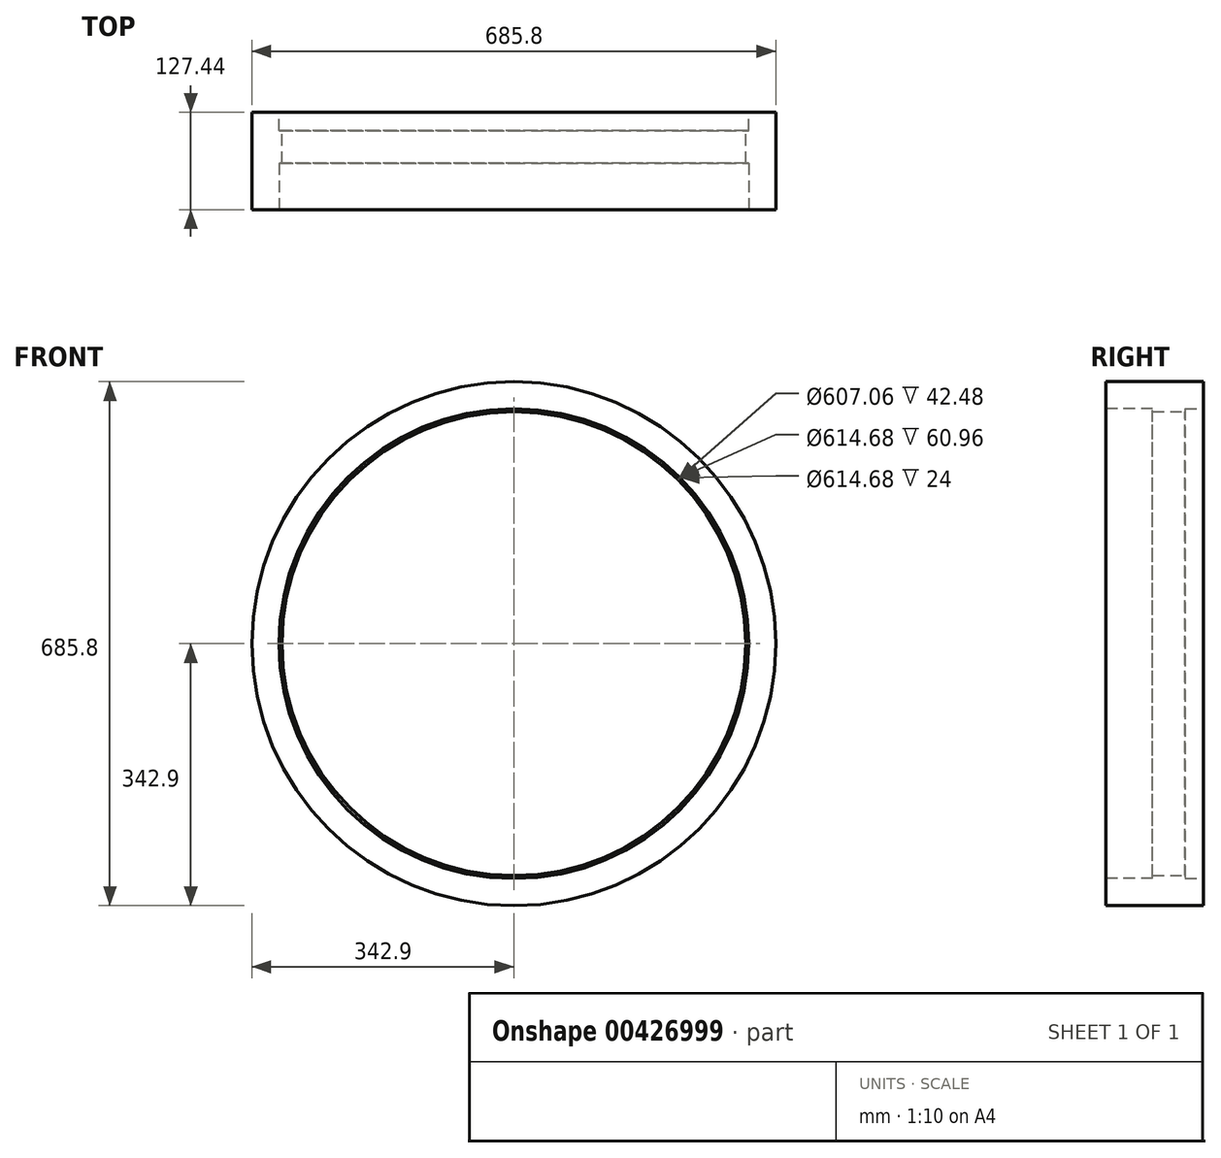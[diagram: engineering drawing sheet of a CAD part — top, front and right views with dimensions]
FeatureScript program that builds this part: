
annotation { "Feature Type Name" : "Feature", "Feature Type Description" : "" }
export const myFeature = defineFeature(function(context is Context, id is Id, definition is map)
    precondition{}
    {
        {
            var Q0;
            Q0=qCreatedBy(makeId("Front.planeOp"),FACE);
            var sketch = newSketch(context, id + "F0", { "sketchPlane" : qUnion([Q0])});
            skCircle(sketch, "E0", {"center": v(0, 0) * mm, "radius": 342.9 * mm});
            skCircle(sketch, "E1", {"center": v(0, 0) * mm, "radius": 303.53 * mm});
            skSolve(sketch);
        }
        {
            var Q0;
            Q0=makeQuery(id+"F0.imprint","IMPRINT",FACE,{"disambiguationData":[TD([[makeQuery(id+"F0.imprint","IMPRINT",EDGE,{"derivedFrom":sQuery(id+"F0.wireOp",EDGE,"E0")}),1.0]])]});
            extrude(context, id + "F1", {"entities" : qUnion([Q0]), "depth" : 91.44 * mm, "hasSecondDirection" : true, "secondDirectionOppositeDirection" : true, "secondDirectionDepth" : 36 * mm});
        }
        {
            var Q0;
            Q0=makeQuery(id+"F1.opExtrude","CAP_FACE",FACE,{"disambiguationData":[OSD([sQuery(id+"F0.wireOp",EDGE,"E0"),sQuery(id+"F0.wireOp",EDGE,"E1")])],"isStart":false});
            var sketch = newSketch(context, id + "F2", { "sketchPlane" : qUnion([Q0])});
            skCircle(sketch, "E2", {"center": v(0, 0) * mm, "radius": 307.34 * mm});
            skSolve(sketch);
        }
        {
            var Q0;
            Q0=makeQuery(id+"F2.imprint","IMPRINT",FACE,{"disambiguationData":[TD([[makeQuery(id+"F2.imprint","IMPRINT",EDGE,{"derivedFrom":sQuery(id+"F2.wireOp",EDGE,"E2")}),1.0]])]});
            extrude(context, id + "F3", {"entities" : qUnion([Q0]), "operationType" : NewBodyOperationType.REMOVE, "oppositeDirection" : true, "depth" : 60.96 * mm});
        }
        {
            var Q0;
            Q0=makeQuery(id+"F1.opExtrude","CAP_FACE",FACE,{"disambiguationData":[OSD([sQuery(id+"F0.wireOp",EDGE,"E0"),sQuery(id+"F0.wireOp",EDGE,"E1")])],"isStart":true});
            var sketch = newSketch(context, id + "F4", { "sketchPlane" : qUnion([Q0])});
            skCircle(sketch, "E3", {"center": v(0, 0) * mm, "radius": 307.34 * mm});
            skSolve(sketch);
        }
        {
            var Q0;
            Q0=makeQuery(id+"F4.imprint","IMPRINT",FACE,{"disambiguationData":[TD([[makeQuery(id+"F4.imprint","IMPRINT",EDGE,{"derivedFrom":sQuery(id+"F4.wireOp",EDGE,"E3")}),1.0]])]});
            extrude(context, id + "F5", {"entities" : qUnion([Q0]), "operationType" : NewBodyOperationType.REMOVE, "oppositeDirection" : true, "depth" : 24 * mm});
        }
    });
